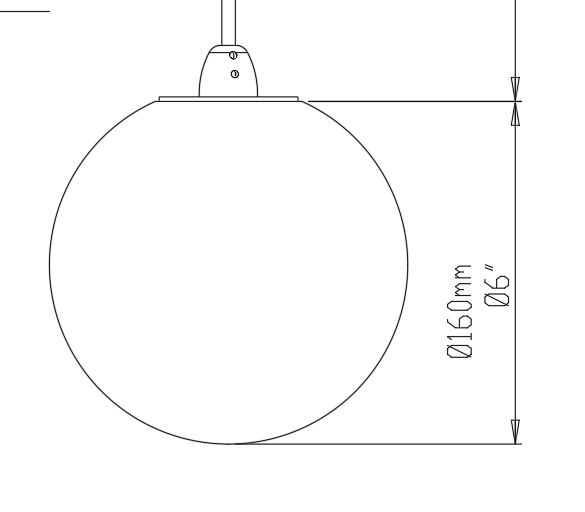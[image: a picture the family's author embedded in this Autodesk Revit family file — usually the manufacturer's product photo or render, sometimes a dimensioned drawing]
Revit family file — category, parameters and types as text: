
# Revit family: GROOVE-Suspension
name_source: partatom
category: Lighting Fixtures
units: mm (PartAtom-declared; Revit-internal decimal feet)

## family parameters
Always vertical = Yes
Cut with Voids When Loaded = No
Host = Ceiling
Light Source = No
OmniClass Number = 23.80.70.11
OmniClass Title = Luminaries for Internal Lighting
Part Type = Normal
Room Calculation Point = No
Round Connector Dimension = Use Diameter
Shared = No

## types (3) — shared parameters
Bulb Diametr = 15 mm  [stored 0.0492126 ft]
Description = SUSPENSION
Designer = Hangar Design Group
Manufacturer = Vistosi
Manufacturer country = Italy
Model = GROOVE
Type Comments = Hangar Design Group
URL = https://vistosi.com
URL Product Page = https://vistosi.it
zero-valued in all types: Default Elevation

## per-type parameters (varying)
| type | Depth | Width |
| GROOVE SP 4 | 60 mm  [stored 0.19685 ft] | 130 mm |
| GROOVE SP 60 | 14 mm  [stored 0.0459318 ft] | 37 mm |
| GROOVE SP 90 | 14 mm  [stored 0.0459318 ft] | 90 mm |

type visibility flags (boolean, named after types; folded from table):
- GROOVE SP 4: Yes: GROOVE SP 4, GROOVE SP 60, GROOVE SP 90
- GROOVE SP 60: Yes: GROOVE SP 60, GROOVE SP 60_Chain
- GROOVE SP 90: Yes: GROOVE SP 90

note: [stored X ft] marks values corroborated as IEEE doubles in the binary element streams (Revit-internal decimal feet)

## geometry (parser evidence)
native form markers: Sweep x13
no freeform markers — native parametric forms only
